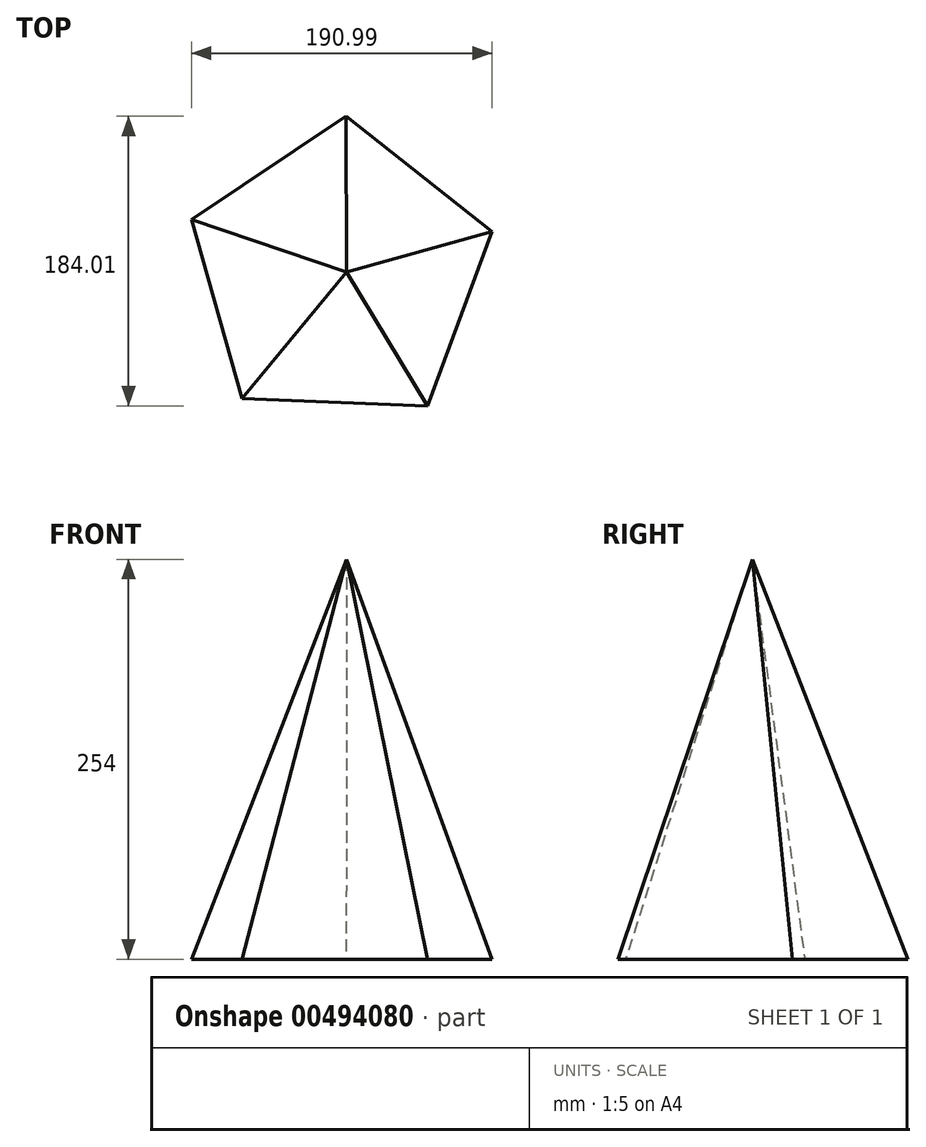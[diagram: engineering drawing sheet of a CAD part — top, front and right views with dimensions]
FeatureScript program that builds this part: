
annotation { "Feature Type Name" : "Feature", "Feature Type Description" : "" }
export const myFeature = defineFeature(function(context is Context, id is Id, definition is map)
    precondition{}
    {
        {
            var Q0;
            Q0=qCreatedBy(makeId("Top.planeOp"),FACE);
            var sketch = newSketch(context, id + "F0", { "sketchPlane" : qUnion([Q0])});
            skCircle(sketch, "E0.cCircle", {"center": v(0, 0) * mm, "radius": 100.5 * mm, "construction": true});
            skLineSegment(sketch, "E0.0", {"start": v(-94.25, 34.86) * mm, "end": v(4.03, 100.41) * mm});
            skLineSegment(sketch, "E0.1", {"start": v(4.03, 100.41) * mm, "end": v(96.74, 27.2) * mm});
            skLineSegment(sketch, "E0.2", {"start": v(96.74, 27.2) * mm, "end": v(55.76, -83.6) * mm});
            skLineSegment(sketch, "E0.3", {"start": v(55.76, -83.6) * mm, "end": v(-62.28, -78.87) * mm});
            skLineSegment(sketch, "E0.4", {"start": v(-62.28, -78.87) * mm, "end": v(-94.25, 34.86) * mm});
            skSolve(sketch);
        }
        {
            var Q0;
            Q0=qCreatedBy(makeId("Top.planeOp"),FACE);
            cPlane(context, id + "F1", {"entities" : qUnion([Q0]), "cplaneType" : CPlaneType.OFFSET, "offset" : 254 * mm, "width" : 152.4 * mm, "height" : 152.4 * mm});
        }
        {
            var Q0;
            Q0=qCreatedBy(id+"F1.planeOp",FACE);
            var sketch = newSketch(context, id + "F2", { "sketchPlane" : qUnion([Q0])});
            skPoint(sketch, "E1", {"position": v(4.13, 1.53) * mm});
            skSolve(sketch);
        }
        {
            var Q0;
            Q0=sQuery(id+"F2.wireOp",VERTEX,"E1");
            var Q1;
            Q1=makeQuery(id+"F0.imprint","IMPRINT",FACE,{"disambiguationData":[TD([[makeQuery(id+"F0.imprint","IMPRINT",EDGE,{"derivedFrom":sQuery(id+"F0.wireOp",EDGE,"E0.0")}),-1.0]])]});
            loft(context, id + "F3", {"sheetProfilesArray" : [{ "sheetProfileEntities" : qUnion([Q0]) }, { "sheetProfileEntities" : qUnion([Q1]) }]});
        }
    });
